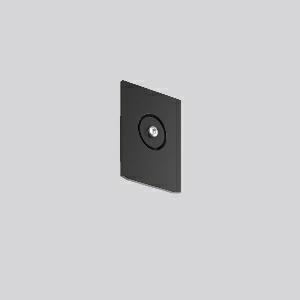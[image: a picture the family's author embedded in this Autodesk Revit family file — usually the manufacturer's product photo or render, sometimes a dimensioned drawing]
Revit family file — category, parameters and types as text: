
# Revit family: linedo_endkappe_s_f_982699_003_e9aa
name_source: partatom
category: Lighting Fixtures
units: mm (PartAtom-declared; Revit-internal decimal feet)

## family parameters
Cut with Voids When Loaded = No
Host = Face
Light Source = No
Part Type = Normal
Room Calculation Point = No
Round Connector Dimension = Use Diameter
Shared = No

## types (1)
- LINEDO_Endkappe_S_F
    Apparent Load = 0 VA
    Default Elevation = 1800 mm
    Description = End cap low profile for LINEDO socket. Plastic end cap to cover the LINEDO plug system at the end of the line. Fastening by TX20 screw. Installation accessories included.
Colour: black
Length: 16 mm
Width: 58 mm
Height: 76 mm
Weight: 21,5 g
    Height = 76 mm
    Lamp = 0 x
    Length = 17 mm
    Luminous efficacy = 0 lm/W
    Manufacturer = RZB
    ModVariant = No
    Model = 982699.003
    Mounting Place = Ceiling
    Mounting Type = Surface mounted, Pendant
    Number of Poles = 1
    OnlyDefault = Yes
    Power Factor = 1
    Product Name = LINEDO_Endkappe_S_F
    Product group = Surface mounted continuous line luminaire system
    ProductGroupID = 310
    Protection Class = Protection class
    Protection Degree = Degree of protection
    RLX_Detail_Level = 1
    RLX_Emergency_Light_Flux = 0 lm
    RLX_Emergency_Type = 0
    RLX_Emergency_Type_DB = No
    RlxData = <blob elided: 9341 chars, md5=bffae8f9>
    Standby Power = 0 W
    System Light Flux = 0 lm
    System Power = 0 W
    Type Comments = Product without accessories
    Type Image = 982699.003.jpg
    URL = http://relux.com
    VarID = ---
    Voltage = 0 V
    Weight = 0.00 kg
    Width = 58 mm

## geometry (parser evidence)
native form markers: Sweep x9
no freeform markers — native parametric forms only
